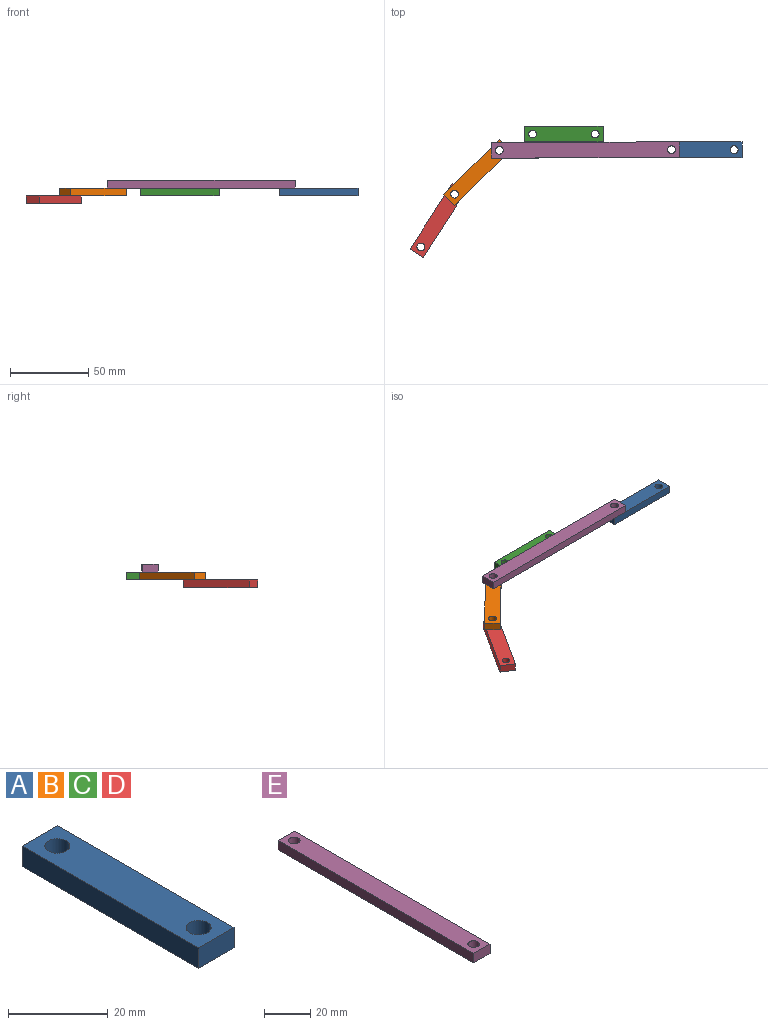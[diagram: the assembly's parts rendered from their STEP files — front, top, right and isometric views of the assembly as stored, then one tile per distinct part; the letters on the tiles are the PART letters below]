
ASSEMBLY  parts=5 mates=4
PART A: 8 faces, bbox 10x50x5 mm
  f0: plane 50x5mm, normal (-1,0,0), area 250mm2, adj f1,f4,f6,f7
  f1: plane 10x5mm, normal (0,-1,0), area 50mm2, adj f0,f2,f6,f7
  f2: plane 50x5mm, normal (1,0,0), area 250mm2, adj f1,f4,f6,f7
  f3: cylinder r=2.5mm len=5mm, axis (0,0,-1), area 78.5mm2, adj f6,f7
  f4: plane 10x5mm, normal (0,1,0), area 50mm2, adj f0,f2,f6,f7
  f5: cylinder r=2.5mm len=5mm, axis (0,0,-1), area 78.5mm2, adj f6,f7
  f6: plane 50x10mm, normal (0,0,1), area 460.7mm2, adj f0,f1,f2,f3,f4,f5
  f7: plane 50x10mm, normal (0,0,-1), area 460.7mm2, adj f0,f1,f2,f3,f4,f5
PART B: same geometry as A
PART C: same geometry as A
PART D: same geometry as A
PART E: 8 faces, bbox 10x120x5 mm
  f0: plane 120x5mm, normal (-1,0,0), area 600mm2, adj f1,f4,f6,f7
  f1: plane 10x5mm, normal (0,-1,0), area 50mm2, adj f0,f2,f6,f7
  f2: plane 120x5mm, normal (1,0,0), area 600mm2, adj f1,f4,f6,f7
  f3: cylinder r=2.5mm len=5mm, axis (0,0,-1), area 78.5mm2, adj f6,f7
  f4: plane 10x5mm, normal (0,1,0), area 50mm2, adj f0,f2,f6,f7
  f5: cylinder r=2.5mm len=5mm, axis (0,0,-1), area 78.5mm2, adj f6,f7
  f6: plane 120x10mm, normal (0,0,1), area 1160.7mm2, adj f0,f1,f2,f3,f4,f5
  f7: plane 120x10mm, normal (0,0,-1), area 1160.7mm2, adj f0,f1,f2,f3,f4,f5
PLACE A rot(axis=(0,0,-1),90deg) t=(100.82,64.16,-0.23)mm
PLACE B rot(axis=(0,0,-1),45.6deg) t=(-39.81,30.85,-0.23)mm
PLACE C rot(axis=(0,0,-1),90deg) t=(12.07,74.16,-0.23)mm fixed
PLACE D rot(axis=(0,0,-1),32.6deg) t=(-61.2,-4.44,-5.23)mm fixed
PLACE E rot(axis=(0,0,-1),89.8deg) t=(-9,6.99,4.77)mm
MATE revolute A.f3 <-> E.f5  axis (0,0,1) through (105.82,59.16,4.77)mm
MATE slider C.f4 <-> A.f4  axis (1,0,0) through (62.07,64.16,4.77)mm
MATE revolute B.f5 <-> E.f3  axis (0,0,1) through (-4.18,58.78,4.77)mm
MATE revolute B.f3 <-> D.f5  axis (0,0,1) through (-32.74,30.78,4.77)mm
